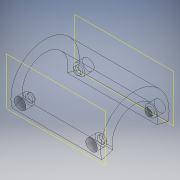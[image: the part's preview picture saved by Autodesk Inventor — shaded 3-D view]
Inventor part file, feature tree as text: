
AUTODESK INVENTOR PART (.ipt)
format: ipt  version: 2018 (Build 220112000, 112)  size: 174,080 bytes
history: native  units: in
note: dims shown in document units (in); Inventor stores cm internally (conversion verified against a paired STEP export)
features: extrude x4, sketch x4, plane x2
ambient origin geometry x8: Origin, YZ Plane, XZ Plane, XY Plane, X Axis, Y Axis, Z Axis, Center Point
bodies: Solid1 (feature_tree)
feature tree (10):
  extrude  "Extrusion1"  Depth=0.5in
  plane  "Work Plane2"
  extrude  "Extrusion7"  Depth=0.25in
  plane  "Work Plane3"
  extrude  "Extrusion8"  TaperAngle=15.0deg  [1 undecoded]
  extrude  "Extrusion9"  Depth=0.2in
  sketch  "Sketch1"  dims[d0=0.75in d1=0.5in]
  sketch  "Sketch10"  dims[d5=0.25in d6=0.25in]
  sketch  "Sketch11"  dims[d7=15.0deg d8=15.0deg]
  sketch  "Sketch12"  dims[d9=1.9685in d10=0.0in d62=0.2in d63=0.2in d64=0.1941in d65=0.1941in d66=0.25in d67=0.25in d68=0.2in d69=0.0in d70=0.2in d71=0.2in d72=0.25in d73=0.25in d74=0.1941in d75=0.1941in d76=0.2in d77=0.0in d78=0.16in d79=0.16in d80=0.1941in d81=0.1941in d82=0.2in d83=0.2in d84=2.0in d85=0.0in]
note: 1 required parameter value undecoded (feature->parameter linkage not recoverable at this tier; creation-order binding heuristic only, values carry confidence <= 0.55)
